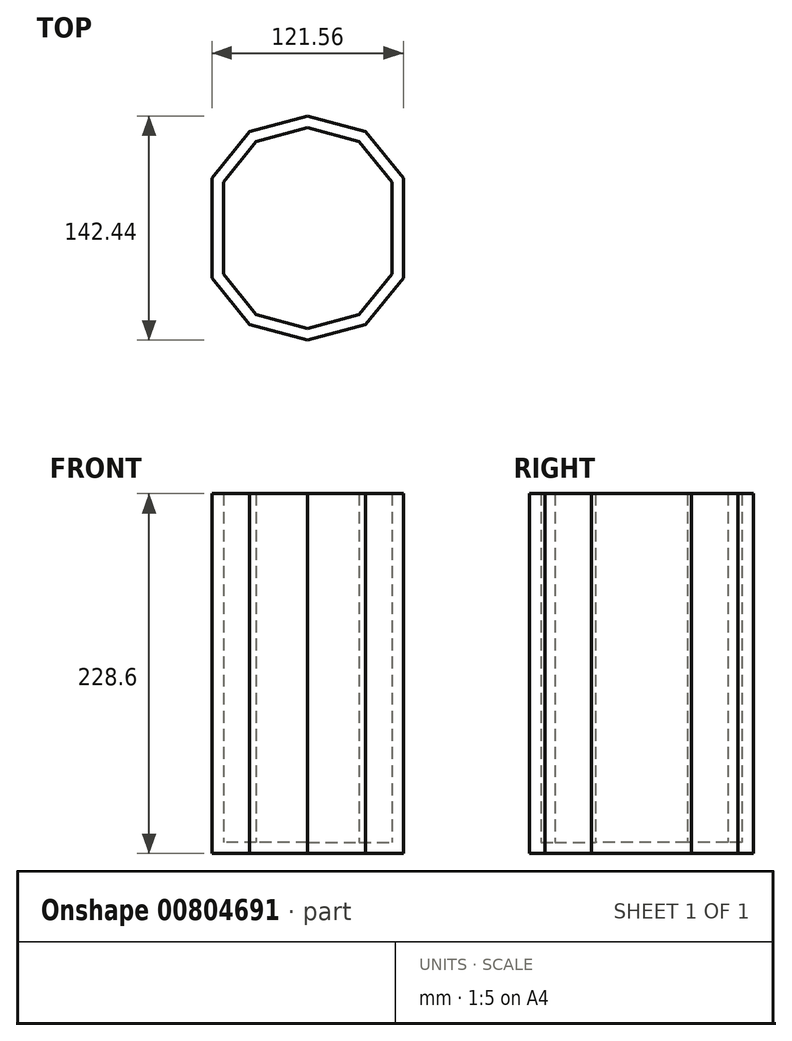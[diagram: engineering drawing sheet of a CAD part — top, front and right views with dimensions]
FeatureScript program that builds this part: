
annotation { "Feature Type Name" : "Feature", "Feature Type Description" : "" }
export const myFeature = defineFeature(function(context is Context, id is Id, definition is map)
    precondition{}
    {
        {
            var Q0;
            Q0=qCreatedBy(makeId("Top.planeOp"),FACE);
            var sketch = newSketch(context, id + "F0", { "sketchPlane" : qUnion([Q0])});
            skLineSegment(sketch, "E0", {"start": v(0, 51.52) * mm, "end": v(0, -124.85) * mm, "construction": true});
            skLineSegment(sketch, "E1", {"start": v(0, 51.52) * mm, "end": v(-36.8, 41.66) * mm});
            skLineSegment(sketch, "E2", {"start": v(-36.8, 41.66) * mm, "end": v(-60.78, 12.05) * mm});
            skLineSegment(sketch, "E3", {"start": v(-60.78, 12.05) * mm, "end": v(-60.78, -51.45) * mm});
            skLineSegment(sketch, "E4.MirrorCS", {"start": v(36.8, 41.66) * mm, "end": v(60.78, 12.05) * mm});
            skLineSegment(sketch, "E5.MirrorCS", {"start": v(0, 51.52) * mm, "end": v(36.8, 41.66) * mm});
            skLineSegment(sketch, "E6.MirrorCS", {"start": v(60.78, 12.05) * mm, "end": v(60.78, -51.45) * mm});
            skLineSegment(sketch, "E7", {"start": v(-60.78, -19.7) * mm, "end": v(60.78, -19.7) * mm, "construction": true});
            skLineSegment(sketch, "E8.MirrorCS", {"start": v(-36.8, -81.06) * mm, "end": v(-60.78, -51.45) * mm});
            skLineSegment(sketch, "E9.MirrorCS", {"start": v(0, -90.92) * mm, "end": v(-36.8, -81.06) * mm});
            skLineSegment(sketch, "E10.MirrorCS", {"start": v(0, -90.92) * mm, "end": v(36.8, -81.06) * mm});
            skLineSegment(sketch, "E11.MirrorCS", {"start": v(36.8, -81.06) * mm, "end": v(60.78, -51.45) * mm});
            skSolve(sketch);
        }
        {
            var Q0;
            Q0=makeQuery(id+"F0.imprint","IMPRINT",FACE,{"disambiguationData":[TD([[makeQuery(id+"F0.imprint","IMPRINT",EDGE,{"derivedFrom":sQuery(id+"F0.wireOp",EDGE,"E1")}),1.0]])]});
            extrude(context, id + "F1", {"entities" : qUnion([Q0]), "depth" : 228.6 * mm, "offsetDistance" : 25.4 * mm});
        }
        {
            var Q0;
            Q0=makeQuery(id+"F1.opExtrude","CAP_FACE",FACE,{"disambiguationData":[OSD([sQuery(id+"F0.wireOp",EDGE,"E1"),sQuery(id+"F0.wireOp",EDGE,"E2"),sQuery(id+"F0.wireOp",EDGE,"E3"),sQuery(id+"F0.wireOp",EDGE,"E4.MirrorCS"),sQuery(id+"F0.wireOp",EDGE,"E5.MirrorCS"),sQuery(id+"F0.wireOp",EDGE,"E6.MirrorCS"),sQuery(id+"F0.wireOp",EDGE,"E8.MirrorCS"),sQuery(id+"F0.wireOp",EDGE,"E9.MirrorCS"),sQuery(id+"F0.wireOp",EDGE,"E10.MirrorCS"),sQuery(id+"F0.wireOp",EDGE,"E11.MirrorCS")])],"isStart":false});
            shell(context, id + "F2", {"entities" : qUnion([Q0]), "thickness" : 7.26 * mm});
        }
    });
